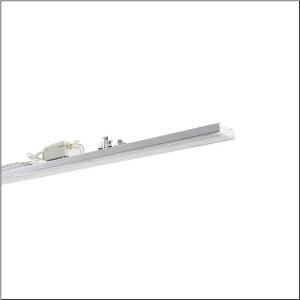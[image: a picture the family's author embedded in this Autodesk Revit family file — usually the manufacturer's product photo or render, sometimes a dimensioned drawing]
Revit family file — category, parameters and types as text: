
# Revit family: licross_11_recessed_ho_51tl12dn4exm3s
name_source: partatom
category: Lighting Fixtures
units: mm (PartAtom-declared; Revit-internal decimal feet)

## family parameters
Cut with Voids When Loaded = No
Host = Face
Light Source = No
Part Type = Normal
Room Calculation Point = No
Round Connector Dimension = Use Diameter
Shared = No

## types (1)
- --- (1 x LED, 1000 lm, 7.2 W, 4000K)
    Apparent Load = 7 VA
    CIE Flux Codes = 66 91 98 100 100
    Color Rendering = 80
    Color Temperature = 4000K
    Default Elevation = 1800 mm
    Description = Licross 11 Recessed HO, luminaire insert, of sheet steel, coil coated, white, length: 1.500mm, width: 66mm, height: 67mm, LED rated luminous flux: 14.030lm, light colour: 840, SDCM (Standard Deviation of Colour Matching)MacAdam ≤ 2 SDCM (initial), control gear: DALI 2 (for two DALI lines), with plug, 6-pole, with phase selection, for trunking rail, 14-core, mains connection: 220..240V, AC, 50/60Hz, rated input power: 81W, for trunking rail, 14-core, internal wiring halogen-free, for emergency light function, converter,control gear: single battery element, battery: LiFePO4, 9Ah, primary optical cover: cover, of PMMA, light emission: direct distribution, primary light characteristic: symmetric, protection rating (complete): IP40, insulation class (complete): insulation class I (protective earthing), certification: CE, UKCA, protection symbol: D if used in an environment without relevant dust loads with corresponding accessories, impact resistance: IK06, permissible ambient temperature for indoor applications: +5..+30°C, standard: EN 60598-2-22, LABS conformity tested according to VDMA 24364:2018-05, reducing of maximum allowable ambient temperature of 5°C with ceiling mounting, corresponds to IFS (International Featured Standards) requirements for safety and quality in the food industry, The light source and the operating device comply with the requirements of the Ecodesign Regulation (EU) 2019/2020 and are replaceable in accordance with this regulation, packaging unit: 1 piece
    Height = 58 mm
    Lamp = 1 x LED
    Lamp Light Flux = 1000 lm
    Lamp Power = 7.2 W
    Lamp count = 1
    Length = 1500 mm
    Luminous efficacy = 139 lm/W
    Manufacturer = Siteco
    ModVariant = No
    Model = 51TL12DN4EXM3S
    Mounting Place = Ceiling
    Mounting Type = Pendant
    Number of Poles = 1
    OnlyDefault = Yes
    Power Factor = 1
    Product Name = Licross 11 Recessed HO
    Product group = luminaire insert | ceiling pendant
    ProductGroupID = 901
    Protection Class = Protection class I
    Protection Degree = IP 40
    RLX_Detail_Level = 1
    RLX_Emergency_Light_Flux = 0 lm
    RLX_Emergency_Type = 0
    RLX_Emergency_Type_DB = No
    RlxData = <blob elided: 25233 chars, md5=cb407894>
    Socket = socket
    Standby Power = 0 W
    System Light Flux = 1000 lm
    System Power = 7 W
    Type Comments = : emergency light operation: 3 h
    Type Image = l_1296930.jpg
    URL = http://relux.com
    VarID = @adj_095485
    Voltage = 0 V
    Weight = 0.00 kg
    Width = 66 mm

## geometry (parser evidence)
native form markers: Blend x4, Sweep x11
no freeform markers — native parametric forms only
